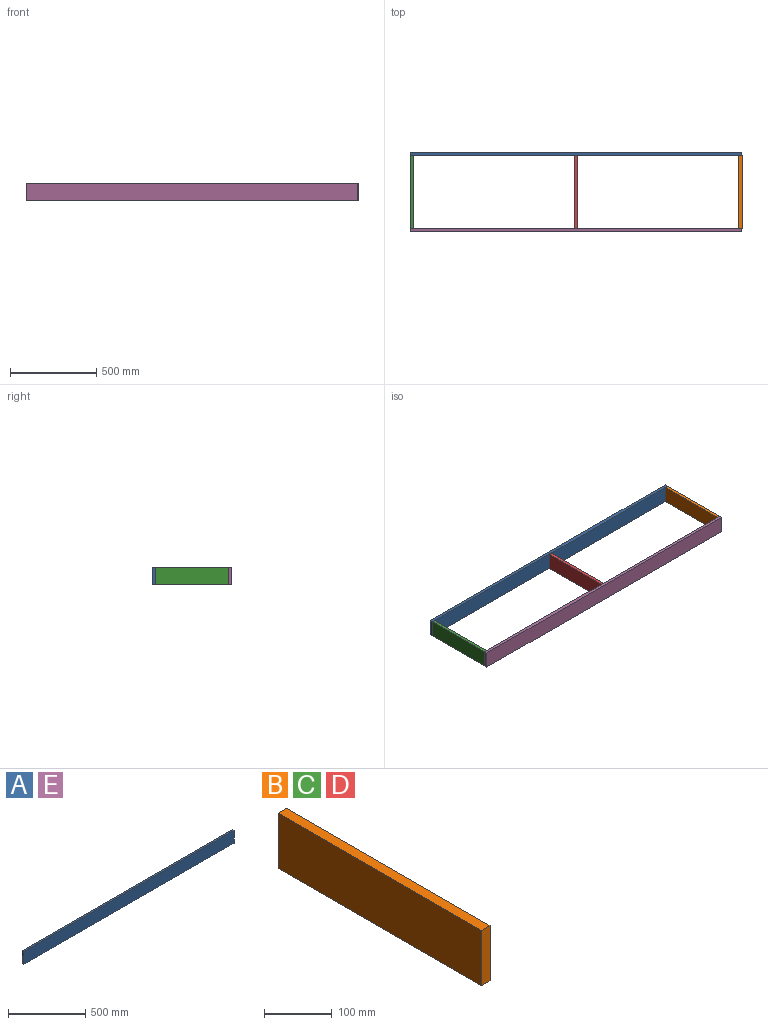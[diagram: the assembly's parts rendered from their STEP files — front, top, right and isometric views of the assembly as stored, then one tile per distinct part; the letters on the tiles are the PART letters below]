
ASSEMBLY  parts=5 mates=12
PART A: 6 faces, bbox 1920x18x100 mm
  f0: plane 100x18mm, normal (-1,0,0), area 1800mm2, adj f1,f3,f4,f5
  f1: plane 1920x18mm, normal (0,0,-1), area 34560mm2, adj f0,f2,f4,f5
  f2: plane 100x18mm, normal (1,0,0), area 1800mm2, adj f1,f3,f4,f5
  f3: plane 1920x18mm, normal (0,0,1), area 34560mm2, adj f0,f2,f4,f5
  f4: plane 1920x100mm, normal (0,-1,0), area 192000mm2, adj f0,f1,f2,f3
  f5: plane 1920x100mm, normal (0,1,0), area 192000mm2, adj f0,f1,f2,f3
PART B: 6 faces, bbox 18x426x100 mm
  f0: plane 100x18mm, normal (0,-1,0), area 1800mm2, adj f1,f3,f4,f5
  f1: plane 426x18mm, normal (0,0,-1), area 7668mm2, adj f0,f2,f4,f5
  f2: plane 100x18mm, normal (0,1,0), area 1800mm2, adj f1,f3,f4,f5
  f3: plane 426x18mm, normal (0,0,1), area 7668mm2, adj f0,f2,f4,f5
  f4: plane 426x100mm, normal (1,0,0), area 42600mm2, adj f0,f1,f2,f3
  f5: plane 426x100mm, normal (-1,0,0), area 42600mm2, adj f0,f1,f2,f3
PART C: same geometry as B
PART D: same geometry as B
PART E: same geometry as A
PLACE A t=(-2050.5,444,0)mm
PLACE B t=(-286.4,209.79,-300.61)mm
PLACE C t=(-2188.4,209.79,-300.61)mm
PLACE D t=(-1234.9,209.79,-300.61)mm
PLACE E t=(-2050.5,0,0)mm
MATE planar A.f4 <-> D.f2  axis (0,-1,0) through (-1228.4,426,-66.65)mm
MATE planar C.f0 <-> E.f5  axis (0,-1,0) through (-2179.4,0,-66.65)mm
MATE planar E.f1 <-> C.f1  axis (0,0,-1) through (-1228.4,-9,-116.65)mm
MATE planar B.f0 <-> E.f5  axis (0,-1,0) through (-277.4,0,-66.65)mm
MATE planar C.f5 <-> E.f0  axis (-1,0,0) through (-2188.4,213,-66.65)mm
MATE planar B.f4 <-> E.f2  axis (1,0,0) through (-268.4,213,-66.65)mm
MATE planar D.f0 <-> E.f5  axis (0,-1,0) through (-1225.9,0,-66.65)mm
MATE planar A.f0 <-> C.f5  axis (-1,0,0) through (-2188.4,435,-66.65)mm
MATE planar A.f1 <-> C.f1  axis (0,0,-1) through (-1228.4,435,-116.65)mm
MATE planar D.f1 <-> E.f1  axis (0,0,-1) through (-1225.9,213,-116.65)mm
MATE planar D.f2 <-> A.f4  axis (0,1,0) through (-1225.9,426,-66.65)mm
MATE planar B.f1 <-> E.f1  axis (0,0,-1) through (-277.4,213,-116.65)mm
